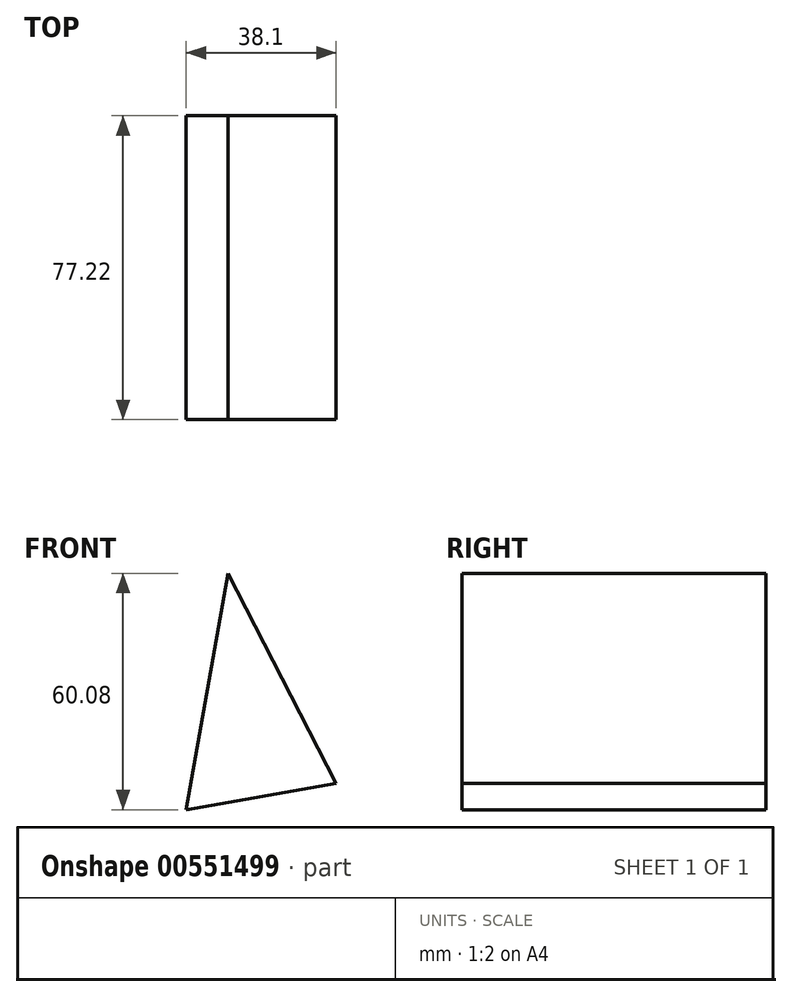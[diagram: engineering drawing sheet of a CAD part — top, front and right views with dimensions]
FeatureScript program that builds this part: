
annotation { "Feature Type Name" : "Feature", "Feature Type Description" : "" }
export const myFeature = defineFeature(function(context is Context, id is Id, definition is map)
    precondition{}
    {
        {
            var Q0;
            Q0=qCreatedBy(makeId("Front.planeOp"),FACE);
            var sketch = newSketch(context, id + "F0", { "sketchPlane" : qUnion([Q0])});
            skLineSegment(sketch, "E0", {"start": v(33.9, 23.82) * mm, "end": v(61.38, -29.62) * mm});
            skLineSegment(sketch, "E1", {"start": v(33.9, 23.82) * mm, "end": v(23.2, -36.65) * mm});
            skLineSegment(sketch, "E2", {"start": v(61.38, -29.62) * mm, "end": v(21.07, -36.65) * mm});
            skLineSegment(sketch, "E3", {"start": v(44.42, -32.58) * mm, "end": v(33.9, 23.82) * mm});
            skSolve(sketch);
        }
        {
            var Q0;
            Q0 = qSketchRegion(id + "F0", true);
            extrude(context, id + "F1", {"entities" : qUnion([Q0]), "depth" : 77.22 * mm, "offsetDistance" : 25.4 * mm});
        }
        {
            var Q0;
            Q0=qCreatedBy(makeId("Front.planeOp"),FACE);
            var sketch = newSketch(context, id + "F2", { "sketchPlane" : qUnion([Q0])});
            skLineSegment(sketch, "E4", {"start": v(34.2, 21.68) * mm, "end": v(43.67, -35.12) * mm});
            skSolve(sketch);
        }
        {
            var Q0;
            Q0=sQuery(id+"F2.wireOp",EDGE,"E4");
            extrude(context, id + "F3", {"bodyType" : ToolBodyType.SURFACE, "surfaceEntities" : qUnion([Q0]), "depth" : 25.4 * mm, "offsetDistance" : 25.4 * mm});
        }
    });
